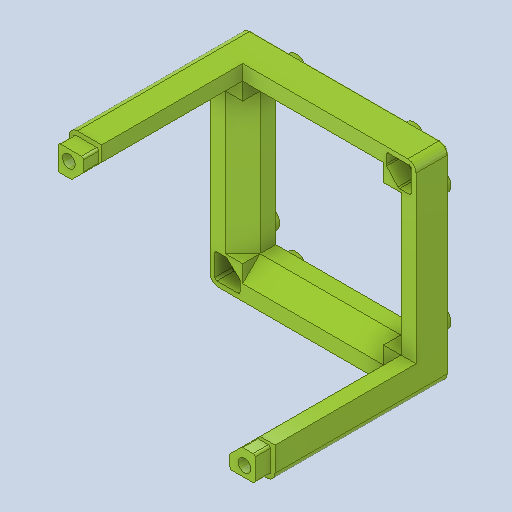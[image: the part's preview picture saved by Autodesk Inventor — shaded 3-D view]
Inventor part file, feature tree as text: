
AUTODESK INVENTOR PART (.ipt)
format: ipt  version: 2023 (Build 270158000, 158)  size: 529,408 bytes
history: native  units: mm
features: projected_geometry x14, extrude x10, sketch x8, plane x4, hole x2, fillet x1
ambient origin geometry x8: Origin, YZ Plane, XZ Plane, XY Plane, X Axis, Y Axis, Z Axis, Center Point
bodies: Solid1 (feature_tree)
feature tree (39):
  extrude  "Extrusion1"  Depth=49.8mm
  extrude  "Extrusion2"  Depth=8.0mm TaperAngle=0.0deg
  hole  "Hole1"  [1 undecoded]
  extrude  "Extrusion3"  Depth=33.8mm TaperAngle=0.0deg
  extrude  "Extrusion4"  Depth=3.65mm
  plane  "Work Plane1"
  extrude  "Extrusion5"  Depth=3.65mm
  extrude  "Extrusion7"  Depth=54.15mm
  extrude  "Extrusion8"  Depth=54.15mm
  fillet  "Fillet2"  [1 undecoded]
  extrude  "Extrusion9"  Depth=3.7mm TaperAngle=0.0deg
  extrude  "Extrusion10"  Depth=4.2mm TaperAngle=0.0deg
  plane  "Work Plane2"
  plane  "Work Plane3"
  hole  "Hole9"  [1 undecoded]
  extrude  "Extrusion11"  Depth=3.4mm
  plane  "Work Plane4"
  sketch  "Sketch1"  dims[d0=49.8mm d1=49.8mm]
  sketch  "Sketch2"  dims[d2=7.88mm d3=8.0mm d4=0.0mm]
  projected_geometry  "Projected Loop1"
  sketch  "Sketch3"  dims[d5=34.1mm d6=0.0mm]
  projected_geometry  "Projected Loop4"
  projected_geometry  "Projected Loop6"
  projected_geometry  "Projected Loop16"
  projected_geometry  "Projected Loop17"
  sketch  "Sketch18"  dims[d8=3.1mm d9=6.0mm d10=5.5mm d11=4.6mm d12=90.0deg d13=16.0mm d14=20.594885mm d30=33.8mm d31=0.0mm]
  sketch  "Sketch19"  dims[d35=33.8mm d36=0.0mm d40=33.8mm d41=0.0mm]
  projected_geometry  "Projected Loop22"
  sketch  "Sketch20"  dims[d96=3.65mm d97=3.65mm]
  projected_geometry  "Projected Loop23"
  sketch  "Sketch21"  dims[d98=3.65mm d99=3.65mm]
  projected_geometry  "Projected Loop24"
  sketch  "Sketch22"  dims[d100=3.65mm d101=3.65mm d102=3.65mm d112=45.0deg d124=3.7mm d125=0.0mm d130=4.2mm d131=0.0mm d132=2.0mm d133=0.5mm d134=3.4mm d135=21.0mm d136=7.38mm d137=3.69mm d138=40.0mm d140=360.0deg d142=4.0mm d143=0.0mm d144=4.95mm d145=2.05mm d146=5.5mm d147=40.0mm d149=360.0deg d151=2.2mm d152=0.0mm d153=3.1mm d154=6.0mm d155=5.5mm d156=3.2mm d157=90.0deg d158=16.0mm d159=20.594885mm d160=5.5mm d161=90.0deg d162=10.0mm d163=0.0mm d164=3.1mm d169=6.1mm d170=6.1mm d171=6.1mm d172=6.1mm d173=1.1mm d174=1.1mm d177=4.18mm d181=4.18mm d182=4.18mm d183=4.18mm d187=54.15mm d188=45.0deg d189=54.15mm d190=135.0deg d191=135.0deg d192=54.15mm d193=54.15mm d194=0.0mm d195=0.0mm]
  projected_geometry  "Projected Loop25"
  projected_geometry  "Projected Loop28"
  projected_geometry  "Projected Loop29"
  projected_geometry  "Projizierte Kontur30"
  projected_geometry  "Projizierte Kontur31"
  projected_geometry  "Projizierte Kontur32"
note: 3 required parameter values undecoded (feature->parameter linkage not recoverable at this tier; creation-order binding heuristic only, values carry confidence <= 0.55)
